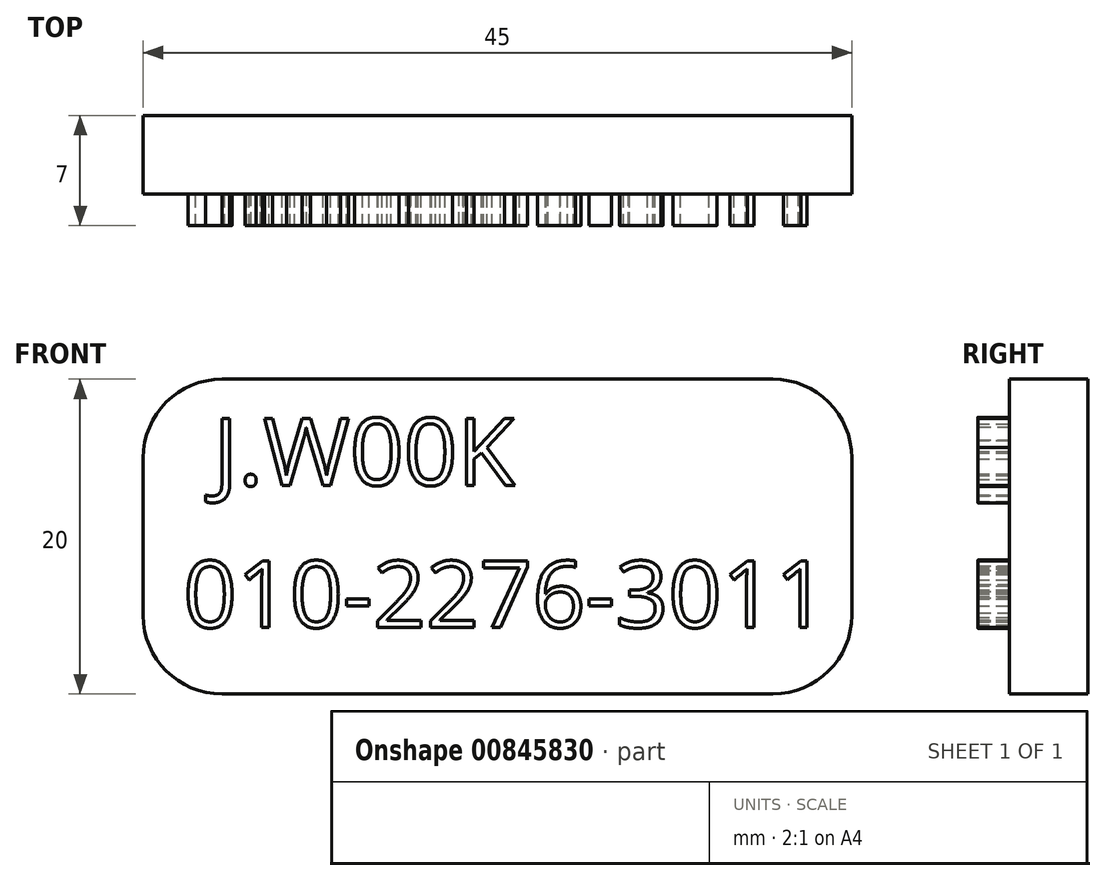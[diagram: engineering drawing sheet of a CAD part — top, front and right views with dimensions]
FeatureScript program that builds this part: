
annotation { "Feature Type Name" : "Feature", "Feature Type Description" : "" }
export const myFeature = defineFeature(function(context is Context, id is Id, definition is map)
    precondition{}
    {
        {
            var Q0;
            Q0=qCreatedBy(makeId("Front.planeOp"),FACE);
            var sketch = newSketch(context, id + "F0", { "sketchPlane" : qUnion([Q0])});
            skLineSegment(sketch, "E0.bottom", {"start": v(0, 0) * mm, "end": v(45, 0) * mm});
            skLineSegment(sketch, "E0.top", {"start": v(0, 20) * mm, "end": v(45, 20) * mm});
            skLineSegment(sketch, "E0.left", {"start": v(0, 0) * mm, "end": v(0, 20) * mm});
            skLineSegment(sketch, "E0.right", {"start": v(45, 0) * mm, "end": v(45, 20) * mm});
            skSolve(sketch);
        }
        {
            var Q0;
            Q0=makeQuery(id+"F0.imprint","IMPRINT",FACE,{"disambiguationData":[TD([[makeQuery(id+"F0.imprint","IMPRINT",EDGE,{"derivedFrom":sQuery(id+"F0.wireOp",EDGE,"E0.bottom")}),1.0]])]});
            extrude(context, id + "F1", {"entities" : qUnion([Q0]), "depth" : 5 * mm, "offsetDistance" : 25 * mm});
        }
        {
            var Q0;
            Q0=makeQuery(id+"F1.opExtrude","SWEPT_EDGE",EDGE,{"disambiguationData":[OSD([sQuery(id+"F0.wireOp",EDGE,"E0.top"),sQuery(id+"F0.wireOp",EDGE,"E0.right")])]});
            var Q1;
            Q1=makeQuery(id+"F1.opExtrude","SWEPT_EDGE",EDGE,{"disambiguationData":[OSD([sQuery(id+"F0.wireOp",EDGE,"E0.top"),sQuery(id+"F0.wireOp",EDGE,"E0.left")])]});
            var Q2;
            Q2=makeQuery(id+"F1.opExtrude","SWEPT_EDGE",EDGE,{"disambiguationData":[OSD([sQuery(id+"F0.wireOp",EDGE,"E0.bottom"),sQuery(id+"F0.wireOp",EDGE,"E0.right")])]});
            var Q3;
            Q3=makeQuery(id+"F1.opExtrude","SWEPT_EDGE",EDGE,{"disambiguationData":[OSD([sQuery(id+"F0.wireOp",EDGE,"E0.bottom"),sQuery(id+"F0.wireOp",EDGE,"E0.left")])]});
            fillet(context, id + "F2", {"entities" : qUnion([Q0, Q1, Q2, Q3]), "radius" : 5 * mm, "tangentPropagation" : true, "allowEdgeOverflow" : false});
        }
        {
            var Q0;
            Q0=makeQuery(id+"F1.opExtrude","CAP_FACE",FACE,{"disambiguationData":[OSD([sQuery(id+"F0.wireOp",EDGE,"E0.bottom"),sQuery(id+"F0.wireOp",EDGE,"E0.top"),sQuery(id+"F0.wireOp",EDGE,"E0.left"),sQuery(id+"F0.wireOp",EDGE,"E0.right")])],"isStart":false});
            var sketch = newSketch(context, id + "F3", { "sketchPlane" : qUnion([Q0])});
            skText(sketch, "E1", { "text": "J.W00K", "fontName": "OpenSans-Regular.ttf"});
            const initialGuessF3  = {"E1": [0.00444, 0.01326, 1, 0, 0.00429]};
            skSetInitialGuess(sketch, initialGuessF3);
            skSolve(sketch);
        }
        {
            var Q0;
            Q0 = qSketchRegion(id + "F3", true);
            extrude(context, id + "F4", {"entities" : qUnion([Q0]), "operationType" : NewBodyOperationType.ADD, "depth" : 2 * mm, "offsetDistance" : 25 * mm});
        }
        {
            var Q0;
            {var subQ0=sQuery(id+"F0.wireOp",EDGE,"E0.right");var subQ1=sQuery(id+"F0.wireOp",EDGE,"E0.top");var subQ2=sQuery(id+"F0.wireOp",EDGE,"E0.left");var subQ3=sQuery(id+"F0.wireOp",EDGE,"E0.bottom");Q0=makeQuery(id+"F4.boolean.opBoolean","SPLIT",FACE,{"disambiguationData":[TD([makeQuery(id+"F1.opExtrude","SWEPT_FACE",FACE,{"disambiguationData":[OSD([subQ3])]})])],"derivedFrom":makeQuery(id+"F1.opExtrude","CAP_FACE",FACE,{"disambiguationData":[OSD([subQ3,subQ1,subQ2,subQ0])],"isStart":false})});}
            var sketch = newSketch(context, id + "F5", { "sketchPlane" : qUnion([Q0])});
            skText(sketch, "E2", { "text": "010-2276-3011", "fontName": "OpenSans-Regular.ttf"});
            const initialGuessF5  = {"E2": [0.00256, 0.00423, 1, 0, 0.00425]};
            skSetInitialGuess(sketch, initialGuessF5);
            skSolve(sketch);
        }
        {
            var Q0;
            Q0 = qSketchRegion(id + "F5", true);
            extrude(context, id + "F6", {"entities" : qUnion([Q0]), "operationType" : NewBodyOperationType.ADD, "depth" : 2 * mm, "offsetDistance" : 25 * mm});
        }
    });
